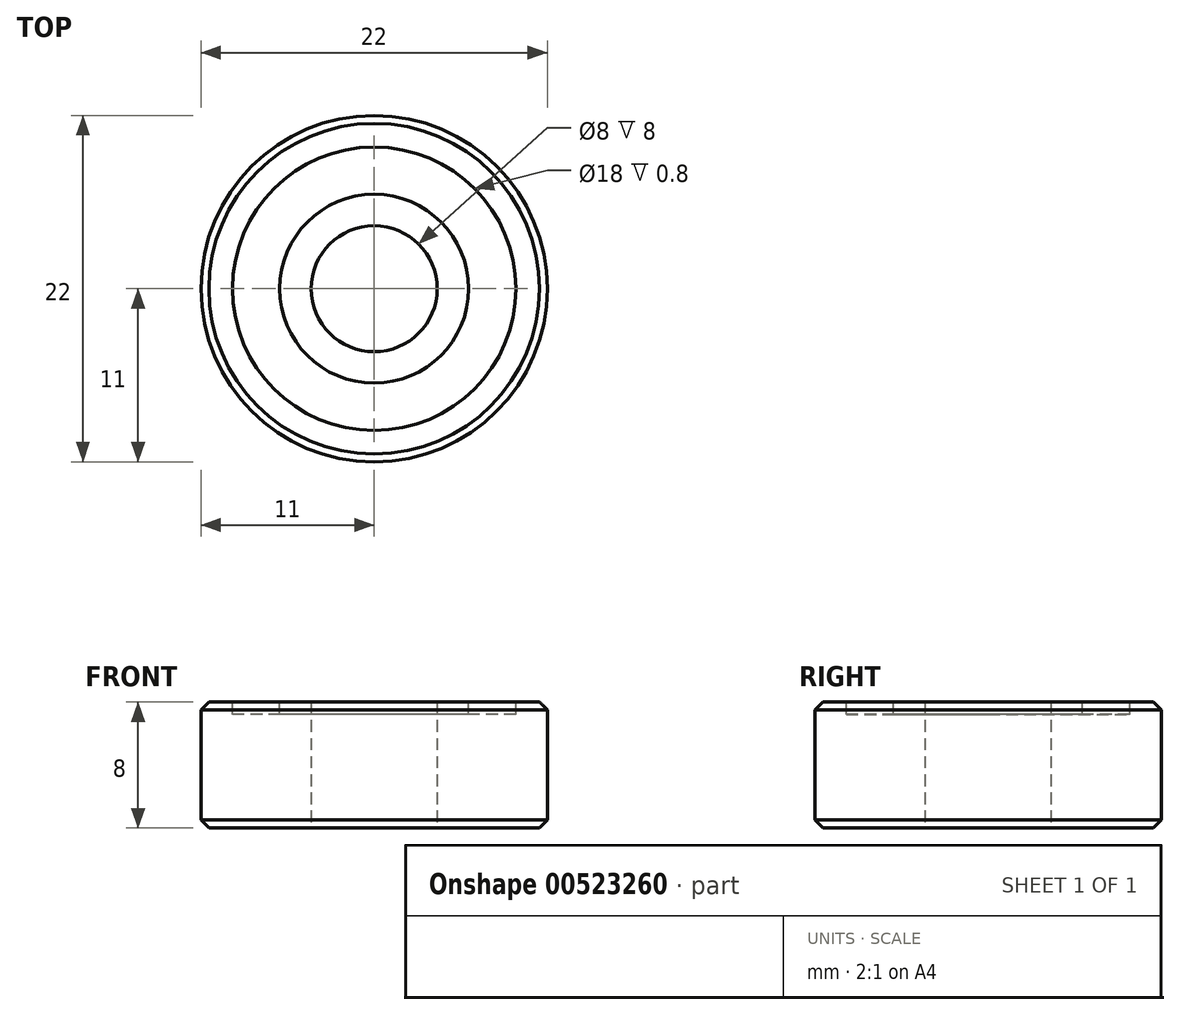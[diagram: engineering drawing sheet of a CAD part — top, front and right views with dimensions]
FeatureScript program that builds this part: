
annotation { "Feature Type Name" : "Feature", "Feature Type Description" : "" }
export const myFeature = defineFeature(function(context is Context, id is Id, definition is map)
    precondition{}
    {
        {
            var Q0;
            Q0=qCreatedBy(makeId("Top.planeOp"),FACE);
            var sketch = newSketch(context, id + "F0", { "sketchPlane" : qUnion([Q0])});
            skCircle(sketch, "E0", {"center": v(0, 0) * mm, "radius": 11 * mm});
            skCircle(sketch, "E1", {"center": v(0, 0) * mm, "radius": 4 * mm});
            skSolve(sketch);
        }
        {
            var Q0;
            Q0 = qSketchRegion(id + "F0", true);
            extrude(context, id + "F1", {"entities" : qUnion([Q0]), "endBound" : BoundingType.SYMMETRIC, "depth" : 8 * mm, "offsetDistance" : 25 * mm});
        }
        {
            var Q0;
            Q0=makeQuery(id+"F1.opExtrude","CAP_FACE",FACE,{"disambiguationData":[OSD([sQuery(id+"F0.wireOp",EDGE,"E0"),sQuery(id+"F0.wireOp",EDGE,"E1")])],"isStart":false});
            var sketch = newSketch(context, id + "F2", { "sketchPlane" : qUnion([Q0])});
            skCircle(sketch, "E2.0", {"center": v(0, 0) * mm, "radius": 6 * mm});
            skCircle(sketch, "E3.0", {"center": v(0, 0) * mm, "radius": 9 * mm});
            skSolve(sketch);
        }
        {
            var Q0;
            Q0=makeQuery(id+"F2.imprint","IMPRINT",FACE,{"disambiguationData":[TD([[makeQuery(id+"F2.imprint","IMPRINT",EDGE,{"derivedFrom":sQuery(id+"F2.wireOp",EDGE,"E2.0")}),-1.0]])]});
            extrude(context, id + "F3", {"entities" : qUnion([Q0]), "operationType" : NewBodyOperationType.REMOVE, "oppositeDirection" : true, "depth" : .8 * mm, "offsetDistance" : 25 * mm});
        }
        {
            var Q0;
            Q0=makeQuery(id+"F1.opExtrude","CAP_EDGE",EDGE,{"disambiguationData":[OSD([sQuery(id+"F0.wireOp",EDGE,"E0")])],"isStart":false});
            var Q1;
            Q1=makeQuery(id+"F1.opExtrude","CAP_EDGE",EDGE,{"disambiguationData":[OSD([sQuery(id+"F0.wireOp",EDGE,"E0")])],"isStart":true});
            chamfer(context, id + "F4", {"entities" : qUnion([Q0, Q1]), "width" : .5 * mm, "tangentPropagation" : true});
        }
    });
